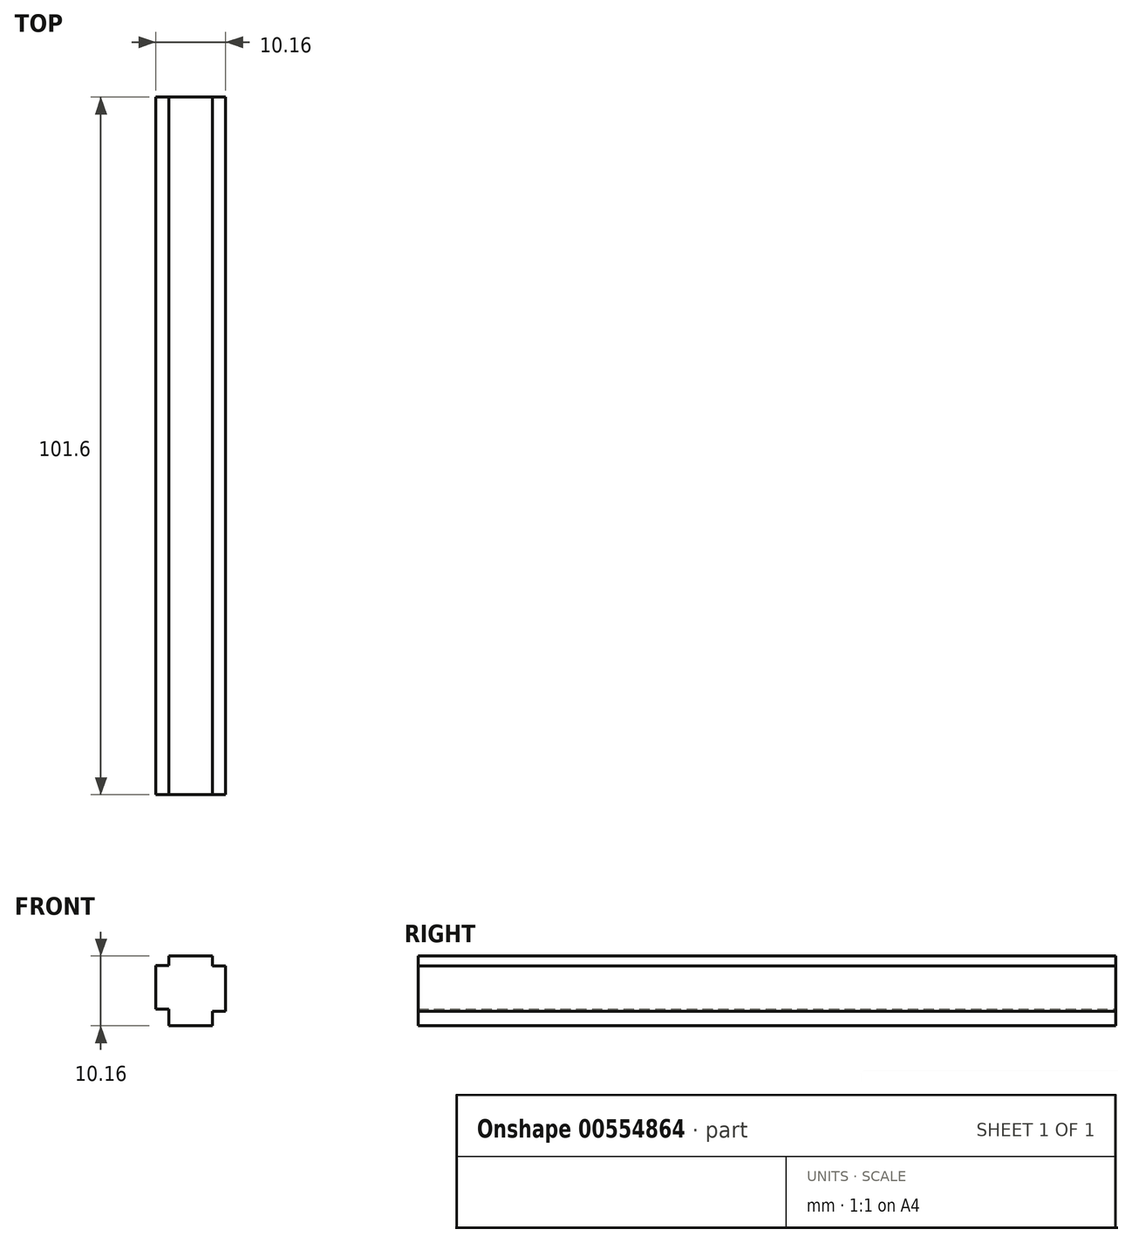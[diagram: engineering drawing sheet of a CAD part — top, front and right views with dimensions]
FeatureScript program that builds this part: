
annotation { "Feature Type Name" : "Feature", "Feature Type Description" : "" }
export const myFeature = defineFeature(function(context is Context, id is Id, definition is map)
    precondition{}
    {
        {
            var Q0;
            Q0=qCreatedBy(makeId("Front.planeOp"),FACE);
            var sketch = newSketch(context, id + "F0", { "sketchPlane" : qUnion([Q0])});
            skPoint(sketch, "E0.start.orphan", {"position": v(0.28, 4.58) * mm});
            skLineSegment(sketch, "E1", {"start": v(0, 4.58) * mm, "end": v(3.18, 4.58) * mm});
            skLineSegment(sketch, "E2", {"start": v(0, 4.58) * mm, "end": v(-3.18, 4.58) * mm});
            skLineSegment(sketch, "E3", {"start": v(0, -5.58) * mm, "end": v(-3.18, -5.58) * mm});
            skLineSegment(sketch, "E4", {"start": v(0, -5.58) * mm, "end": v(3.18, -5.58) * mm});
            skLineSegment(sketch, "E5", {"start": v(-5.08, 0) * mm, "end": v(-5.08, 3.17) * mm});
            skLineSegment(sketch, "E6", {"start": v(5.08, 0) * mm, "end": v(5.08, 3.16) * mm});
            skLineSegment(sketch, "E7", {"start": v(5.08, 0) * mm, "end": v(5.08, -3.16) * mm});
            skLineSegment(sketch, "E8", {"start": v(-5.08, 3.17) * mm, "end": v(-3.18, 3.17) * mm});
            skLineSegment(sketch, "E9", {"start": v(-3.18, 3.17) * mm, "end": v(-3.18, 4.58) * mm});
            skLineSegment(sketch, "E10", {"start": v(3.18, -5.58) * mm, "end": v(3.18, -3.5) * mm});
            skLineSegment(sketch, "E11", {"start": v(3.18, -3.5) * mm, "end": v(5.08, -3.5) * mm});
            skLineSegment(sketch, "E12", {"start": v(5.08, -3.5) * mm, "end": v(5.08, -3.16) * mm});
            skLineSegment(sketch, "E13", {"start": v(3.18, 4.58) * mm, "end": v(3.18, 3.12) * mm});
            skLineSegment(sketch, "E14", {"start": v(3.18, 3.12) * mm, "end": v(5.08, 3.16) * mm});
            skLineSegment(sketch, "E15", {"start": v(-5.08, 0) * mm, "end": v(-5.08, -3.17) * mm});
            skLineSegment(sketch, "E16", {"start": v(-5.08, -3.17) * mm, "end": v(-3.18, -3.17) * mm});
            skLineSegment(sketch, "E17", {"start": v(-3.18, -3.17) * mm, "end": v(-3.18, -5.58) * mm});
            skPoint(sketch, "E18.start.orphan", {"position": v(-3.66, -5.58) * mm});
            skSolve(sketch);
        }
        {
            var Q0;
            Q0=makeQuery(id+"F0.imprint","IMPRINT",FACE,{"disambiguationData":[TD([[makeQuery(id+"F0.imprint","IMPRINT",EDGE,{"derivedFrom":sQuery(id+"F0.wireOp",EDGE,"E1")}),-1.0]])]});
            extrude(context, id + "F1", {"entities" : qUnion([Q0]), "depth" : 101.6 * mm, "offsetDistance" : 25.4 * mm});
        }
    });
